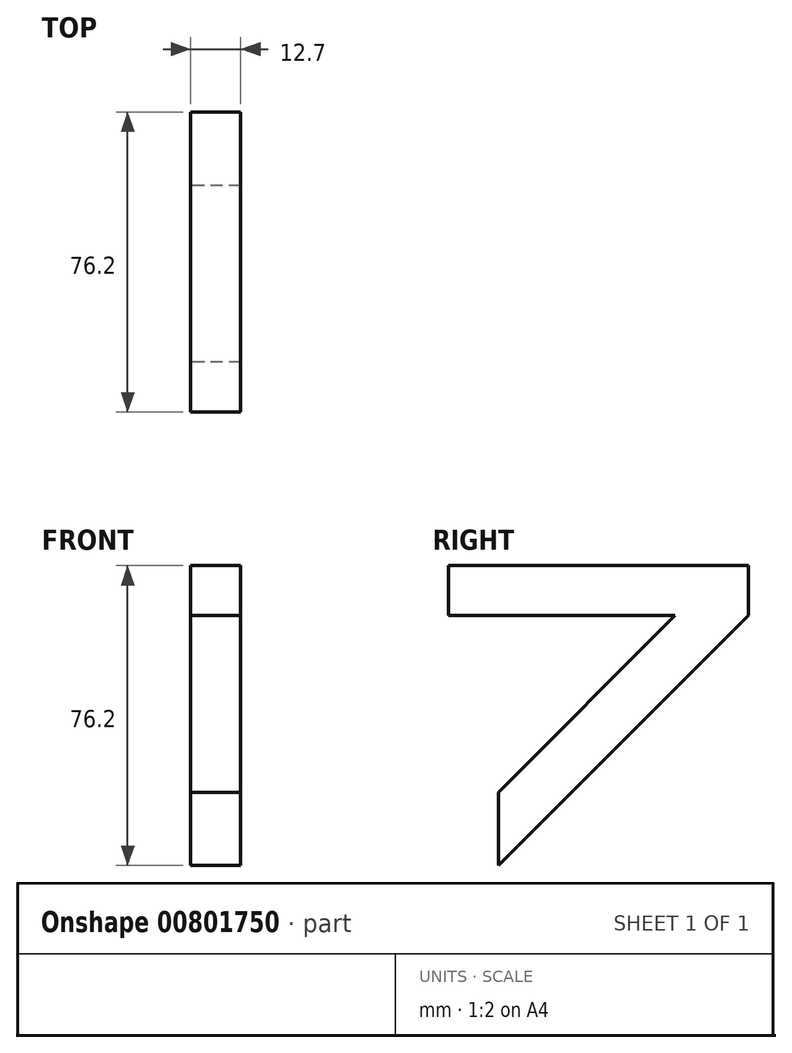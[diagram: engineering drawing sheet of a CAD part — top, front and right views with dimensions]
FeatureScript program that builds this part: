
annotation { "Feature Type Name" : "Feature", "Feature Type Description" : "" }
export const myFeature = defineFeature(function(context is Context, id is Id, definition is map)
    precondition{}
    {
        {
            var Q0;
            Q0=qCreatedBy(makeId("Right.planeOp"),FACE);
            var sketch = newSketch(context, id + "F0", { "sketchPlane" : qUnion([Q0])});
            skLineSegment(sketch, "E0.bottom", {"start": v(76.2, 0) * mm, "end": v(0, 0) * mm});
            skLineSegment(sketch, "E0.top", {"start": v(76.2, -12.7) * mm, "end": v(0, -12.7) * mm});
            skLineSegment(sketch, "E0.left", {"start": v(76.2, 0) * mm, "end": v(76.2, -12.7) * mm});
            skLineSegment(sketch, "E0.right", {"start": v(0, 0) * mm, "end": v(0, -12.7) * mm});
            skLineSegment(sketch, "E1.bottom", {"start": v(0, -12.7) * mm, "end": v(12.7, -12.7) * mm});
            skLineSegment(sketch, "E1.top", {"start": v(0, -82.55) * mm, "end": v(12.7, -82.55) * mm});
            skLineSegment(sketch, "E1.left", {"start": v(0, -12.7) * mm, "end": v(0, -82.55) * mm});
            skLineSegment(sketch, "E1.right", {"start": v(12.7, -12.7) * mm, "end": v(12.7, -82.55) * mm});
            skLineSegment(sketch, "E2", {"start": v(12.7, -76.2) * mm, "end": v(76.2, -12.7) * mm});
            skLineSegment(sketch, "E3", {"start": v(76.2, -12.7) * mm, "end": v(57.6, -12.7) * mm});
            skLineSegment(sketch, "E4", {"start": v(57.6, -12.7) * mm, "end": v(12.7, -57.6) * mm});
            skLineSegment(sketch, "E5", {"start": v(12.7, -57.6) * mm, "end": v(12.7, -76.2) * mm});
            skSolve(sketch);
        }
        {
            var Q0;
            {var subQ1=sQuery(id+"F0.wireOp",EDGE,"E1.bottom");Q0=makeQuery(id+"F0.imprint","IMPRINT",FACE,{"disambiguationData":[TD([[makeQuery(id+"F0.imprint","IMPRINT",EDGE,{"derivedFrom":subQ1}),-1.0]])]});}
            var Q1;
            Q1=makeQuery(id+"F0.imprint","IMPRINT",FACE,{"disambiguationData":[TD([[makeQuery(id+"F0.imprint","IMPRINT",EDGE,{"derivedFrom":sQuery(id+"F0.wireOp",EDGE,"E0.bottom")}),1.0]])]});
            var Q2;
            Q2=makeQuery(id+"F0.imprint","IMPRINT",FACE,{"disambiguationData":[TD([[makeQuery(id+"F0.imprint","IMPRINT",EDGE,{"derivedFrom":sQuery(id+"F0.wireOp",EDGE,"E2")}),1.0]])]});
            extrude(context, id + "F1", {"entities" : qUnion([Q0, Q1, Q2]), "depth" : 12.7 * mm, "offsetDistance" : 25.4 * mm});
        }
    });
